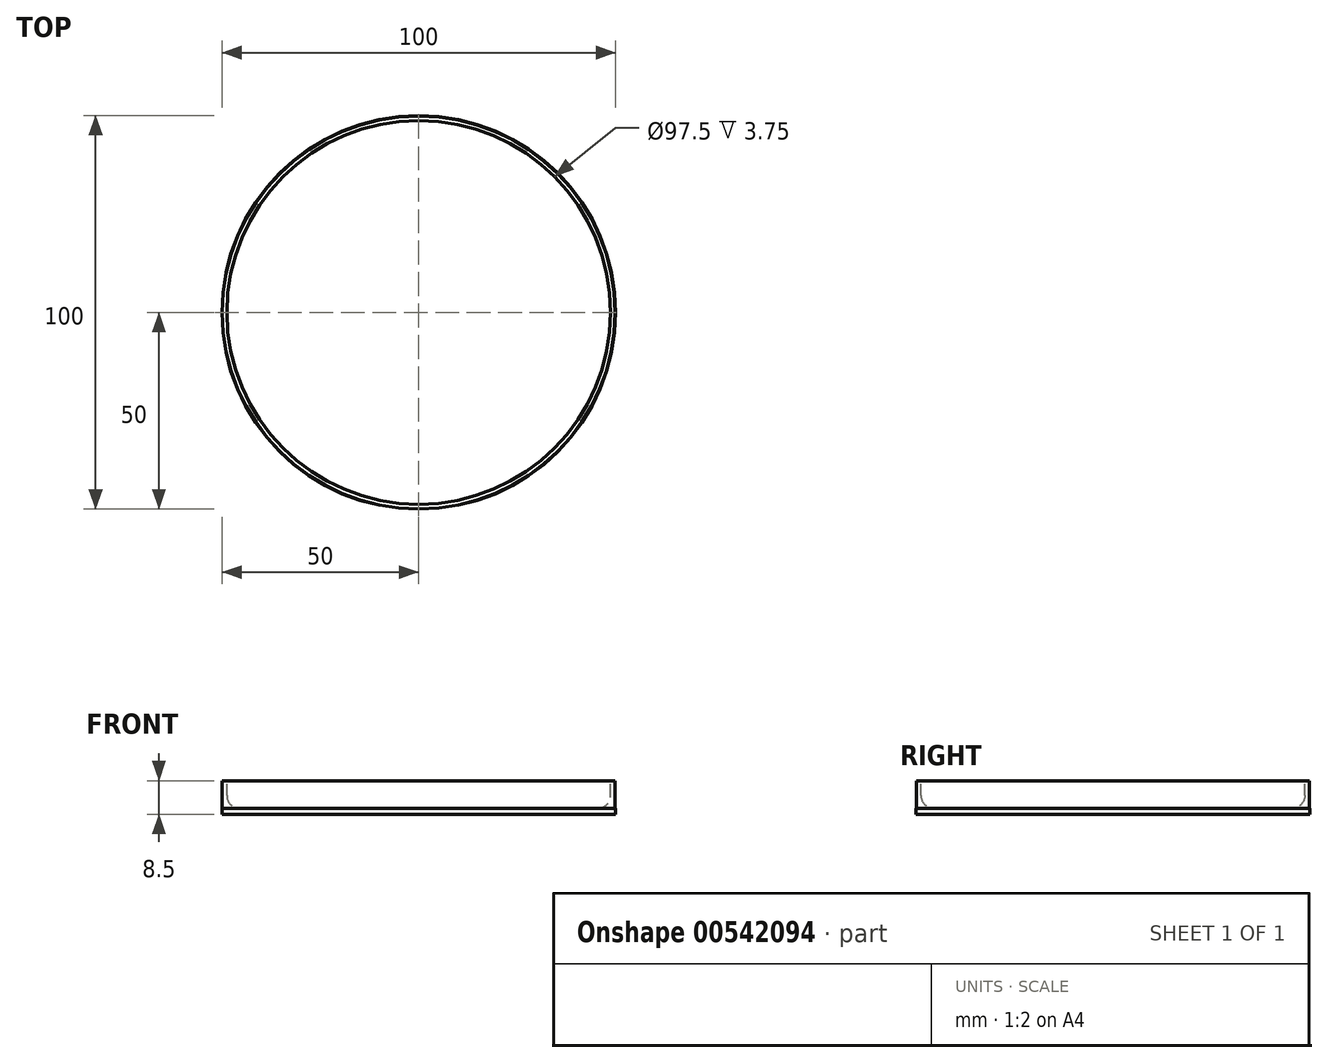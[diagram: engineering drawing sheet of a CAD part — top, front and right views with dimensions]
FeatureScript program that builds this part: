
annotation { "Feature Type Name" : "Feature", "Feature Type Description" : "" }
export const myFeature = defineFeature(function(context is Context, id is Id, definition is map)
    precondition{}
    {
        {
            var Q0;
            Q0=qCreatedBy(makeId("Top.planeOp"),FACE);
            var sketch = newSketch(context, id + "F0", { "sketchPlane" : qUnion([Q0])});
            skCircle(sketch, "E0", {"center": v(0, 0) * mm, "radius": 50 * mm});
            skPoint(sketch, "E1", {"position": v(-45.5, 0) * mm});
            skSolve(sketch);
        }
        {
            var Q0;
            Q0 = qSketchRegion(id + "F0", true);
            extrude(context, id + "F1", {"entities" : qUnion([Q0]), "depth" : 1.5 * mm, "offsetDistance" : 25 * mm});
        }
        {
            var Q0;
            Q0=qCreatedBy(makeId("Front.planeOp"),FACE);
            var sketch = newSketch(context, id + "F2", { "sketchPlane" : qUnion([Q0])});
            skLineSegment(sketch, "E2.bottom", {"start": v(-49.9, 0) * mm, "end": v(-48.75, 0) * mm});
            skLineSegment(sketch, "E2.top", {"start": v(-49.9, 8.5) * mm, "end": v(-48.75, 8.5) * mm});
            skLineSegment(sketch, "E2.left", {"start": v(-48.75, 4.75) * mm, "end": v(-48.75, 8.5) * mm});
            skLineSegment(sketch, "E2.right", {"start": v(-49.9, 0) * mm, "end": v(-49.9, 8.5) * mm});
            skLineSegment(sketch, "E3", {"start": v(-45.5, 0) * mm, "end": v(-45.5, 1.5) * mm});
            skLineSegment(sketch, "E4", {"start": v(-45.5, 1.5) * mm, "end": v(-45.5, 1.5) * mm});
            skPoint(sketch, "E5.newPointA", {"position": v(-48.75, 1.5) * mm});
            skArc(sketch, "E5.filletArc", {"start": v(-48.75, 4.75) * mm, "mid": v(-47.8, 2.45) * mm, "end": v(-45.5, 1.5) * mm});
            skLineSegment(sketch, "E6", {"start": v(-48.75, 0) * mm, "end": v(-45.5, 0) * mm});
            skSolve(sketch);
        }
        {
            var Q0;
            Q0 = qSketchRegion(id + "F2", true);
            var Q1;
            Q1=makeQuery(id+"F1.opExtrude","SWEPT_FACE",FACE,{"disambiguationData":[OSD([sQuery(id+"F0.wireOp",EDGE,"E0")])]});
            revolve(context, id + "F3", {"operationType" : NewBodyOperationType.ADD, "entities" : qUnion([Q0]), "axis" : qUnion([Q1]), "revolveType" : RevolveType.FULL});
        }
    });
